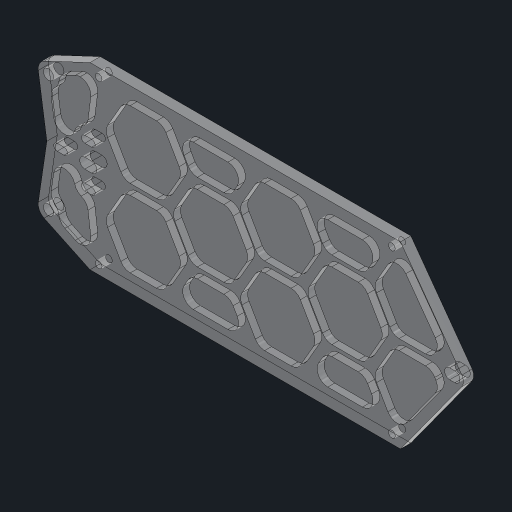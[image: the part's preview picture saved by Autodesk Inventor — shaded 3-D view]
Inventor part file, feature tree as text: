
AUTODESK INVENTOR PART (.ipt)
format: ipt  version: 2023.2 (Build 272271030, 271C)  size: 605,696 bytes
history: native  units: mm
features: extrude x2, sketch x2, mirror x1, fillet x1, projected_geometry x1
ambient origin geometry x8: Origin, YZ Plane, XZ Plane, XY Plane, X Axis, Y Axis, Z Axis, Center Point
bodies: Solid1 (feature_tree)
feature tree (7):
  extrude  "Extrusion1"  Depth=42.0mm
  extrude  "Extrusion6"  Depth=22.0mm
  mirror  "Mirror2"
  fillet  "Fillet4"  Radius=36.0mm
  sketch  "Sketch1"  dims[d0=90.0mm d1=42.0mm]
  sketch  "Sketch6"  dims[d2=5.0mm d3=22.0mm d5=36.0mm d6=127.0mm d7=8.0mm d8=8.0mm d9=4.0mm d10=3.0mm d11=3.0mm d12=8.0mm d13=3.0mm d14=1.5mm d15=8.5mm d16=1.25mm d17=5.0mm d18=5.0mm d19=1.0mm d20=3.0mm d21=16.0mm d22=12.0mm d23=1.0mm d24=1.0mm d25=1.0mm d26=2.0mm d27=1.0mm d28=2.0mm d29=2.0mm d30=2.0mm d31=2.0mm d32=2.0mm d33=1.0mm d34=5.0mm d35=5.0mm d36=5.0mm d37=1.5mm d38=1.5mm d39=3.0mm d40=0.0mm d102=2.0mm d103=2.5mm d104=2.5mm d105=2.5mm d106=2.5mm d111=3.0mm d113=5.0mm d114=3.0mm d115=5.0mm d116=2.0mm d117=2.0mm d118=2.0mm d119=2.0mm d120=6.2mm d121=3.0mm d122=3.0mm d123=3.0mm d124=3.0mm d125=1.5mm d126=3.0mm d127=3.0mm d128=38.971143mm d129=2.0mm d130=0.0mm d131=30.0mm d133=38.971143mm d134=10.0mm d136=10.0mm d138=3.1mm]
  projected_geometry  "Projected Loop6"
